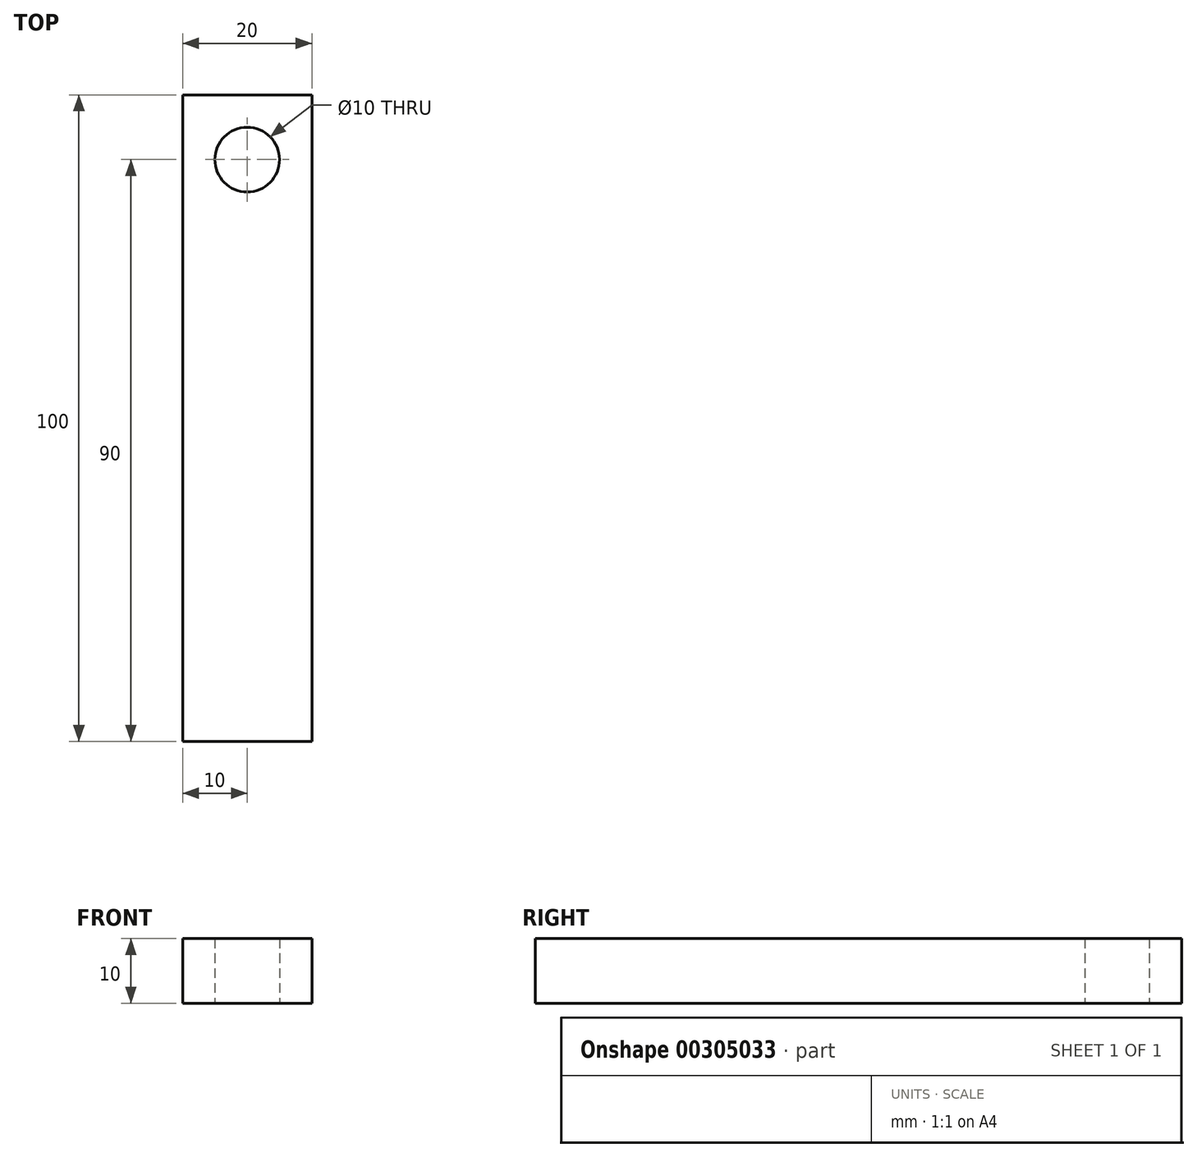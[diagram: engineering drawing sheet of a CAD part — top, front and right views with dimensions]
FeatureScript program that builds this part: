
annotation { "Feature Type Name" : "Feature", "Feature Type Description" : "" }
export const myFeature = defineFeature(function(context is Context, id is Id, definition is map)
    precondition{}
    {
        {
            var Q0;
            Q0=qCreatedBy(makeId("Top.planeOp"),FACE);
            var sketch = newSketch(context, id + "F0", { "sketchPlane" : qUnion([Q0])});
            skLineSegment(sketch, "E0.bottom", {"start": v(0, 0) * mm, "end": v(20, 0) * mm});
            skLineSegment(sketch, "E0.top", {"start": v(0, -100) * mm, "end": v(20, -100) * mm});
            skLineSegment(sketch, "E0.left", {"start": v(0, 0) * mm, "end": v(0, -100) * mm});
            skLineSegment(sketch, "E0.right", {"start": v(20, 0) * mm, "end": v(20, -100) * mm});
            skCircle(sketch, "E1", {"center": v(10, -10) * mm, "radius": 5 * mm});
            skSolve(sketch);
        }
        {
            var Q0;
            Q0 = qSketchRegion(id + "F0", true);
            extrude(context, id + "F1", {"entities" : qUnion([Q0]), "depth" : 10 * mm});
        }
    });
